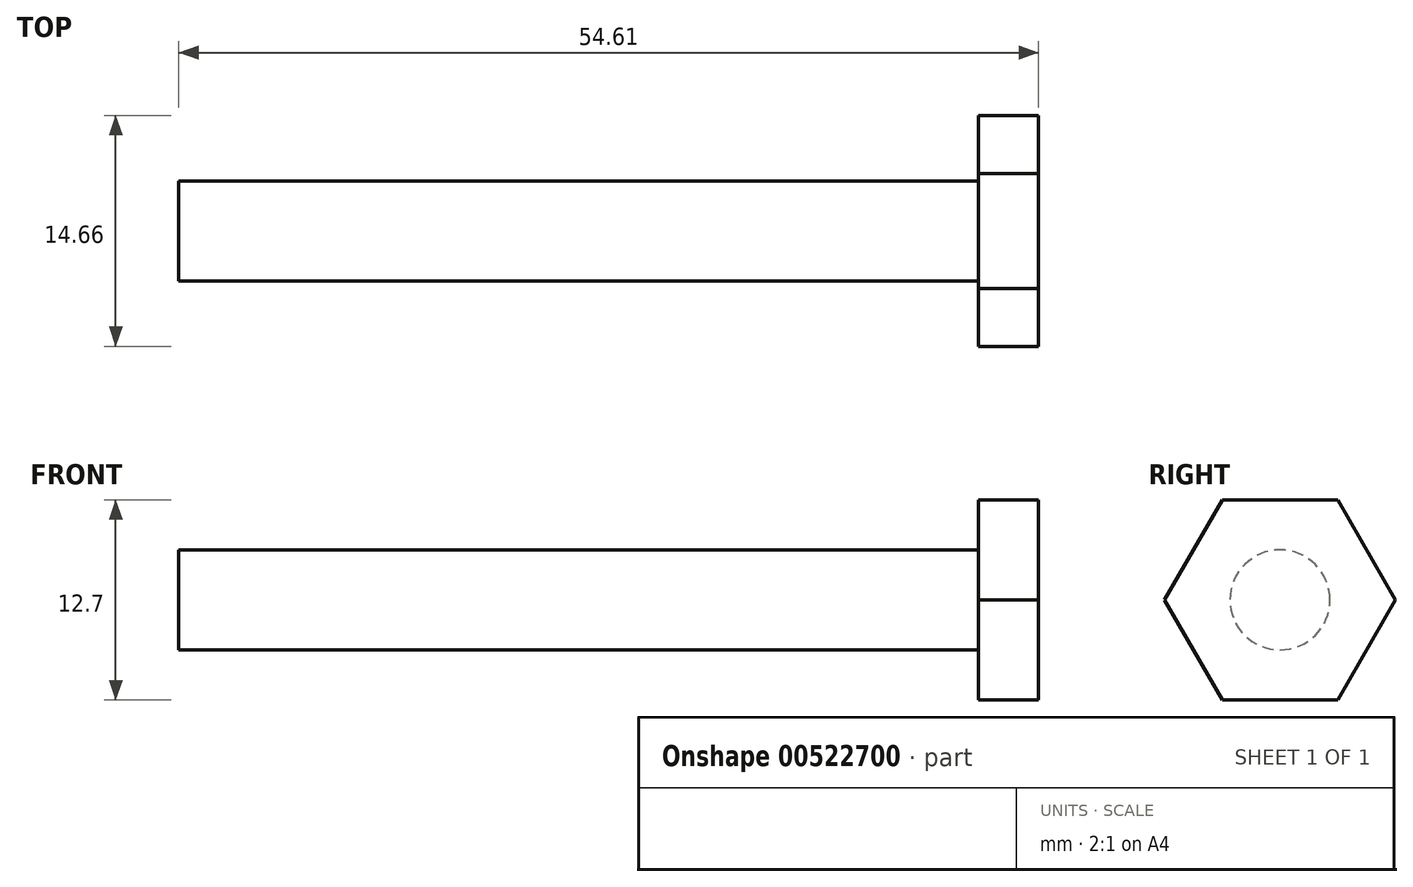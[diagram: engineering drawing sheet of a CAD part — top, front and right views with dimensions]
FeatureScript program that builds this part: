
annotation { "Feature Type Name" : "Feature", "Feature Type Description" : "" }
export const myFeature = defineFeature(function(context is Context, id is Id, definition is map)
    precondition{}
    {
        {
            var Q0;
            Q0=qCreatedBy(makeId("Right.planeOp"),FACE);
            var sketch = newSketch(context, id + "F0", { "sketchPlane" : qUnion([Q0])});
            skCircle(sketch, "E0.cCircle", {"center": v(0, 0) * mm, "radius": 6.35 * mm, "construction": true});
            skLineSegment(sketch, "E0.0", {"start": v(3.67, -6.35) * mm, "end": v(-3.67, -6.35) * mm});
            skLineSegment(sketch, "E0.1", {"start": v(-3.67, -6.35) * mm, "end": v(-7.33, 0) * mm});
            skLineSegment(sketch, "E0.2", {"start": v(-7.33, 0) * mm, "end": v(-3.67, 6.35) * mm});
            skLineSegment(sketch, "E0.3", {"start": v(-3.67, 6.35) * mm, "end": v(3.67, 6.35) * mm});
            skLineSegment(sketch, "E0.4", {"start": v(3.67, 6.35) * mm, "end": v(7.33, 0) * mm});
            skLineSegment(sketch, "E0.5", {"start": v(7.33, 0) * mm, "end": v(3.67, -6.35) * mm});
            skPoint(sketch, "E0.0.midPoint", {"position": v(0, -6.35) * mm});
            skSolve(sketch);
        }
        {
            var Q0;
            Q0=qSketchRegion(id+"F0",true);
            extrude(context, id + "F1", {"entities" : qUnion([Q0]), "depth" : 3.8 * mm, "offsetDistance" : 25.4 * mm});
        }
        {
            var Q0;
            Q0=qCreatedBy(makeId("Right.planeOp"),FACE);
            var sketch = newSketch(context, id + "F2", { "sketchPlane" : qUnion([Q0])});
            skCircle(sketch, "E1", {"center": v(0, 0) * mm, "radius": 3.18 * mm});
            skSolve(sketch);
        }
        {
            var Q0;
            Q0=qSketchRegion(id+"F2",true);
            extrude(context, id + "F3", {"entities" : qUnion([Q0]), "operationType" : NewBodyOperationType.ADD, "oppositeDirection" : true, "depth" : 50.8 * mm, "offsetDistance" : 25.4 * mm});
        }
    });
